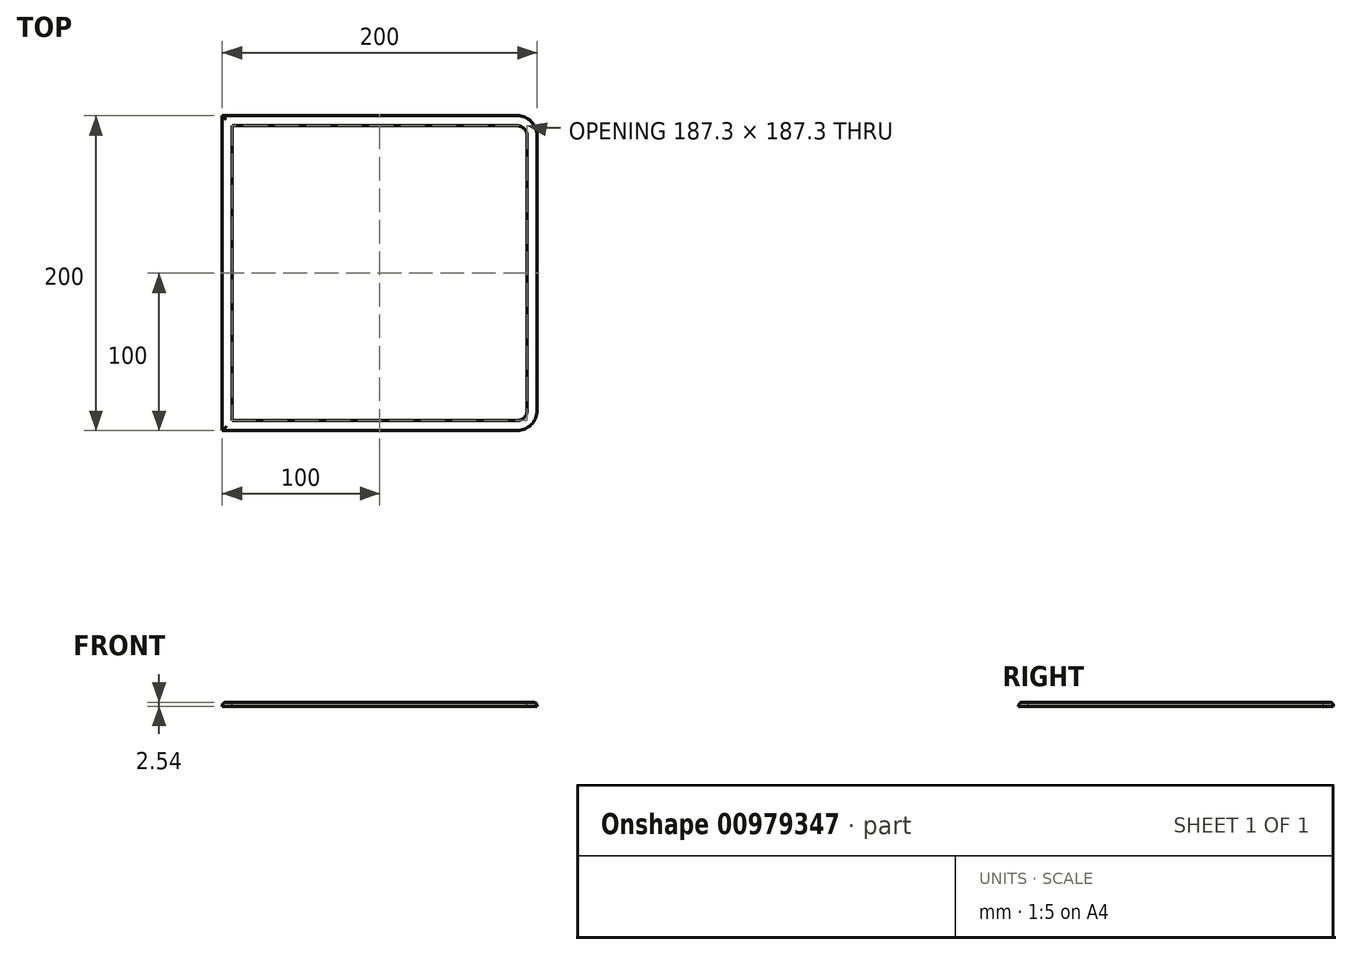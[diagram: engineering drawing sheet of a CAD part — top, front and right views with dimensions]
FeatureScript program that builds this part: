
annotation { "Feature Type Name" : "Feature", "Feature Type Description" : "" }
export const myFeature = defineFeature(function(context is Context, id is Id, definition is map)
    precondition{}
    {
        {
            var Q0;
            Q0=qCreatedBy(makeId("Top.planeOp"),FACE);
            var sketch = newSketch(context, id + "F0", { "sketchPlane" : qUnion([Q0])});
            skLineSegment(sketch, "E0.bottom", {"start": v(0, 0) * mm, "end": v(200, 0) * mm});
            skLineSegment(sketch, "E0.top", {"start": v(0, 200) * mm, "end": v(200, 200) * mm});
            skLineSegment(sketch, "E0.left", {"start": v(0, 0) * mm, "end": v(0, 200) * mm});
            skLineSegment(sketch, "E0.right", {"start": v(200, 0) * mm, "end": v(200, 200) * mm});
            skSolve(sketch);
        }
        {
            var Q0;
            Q0=makeQuery(id+"F0.imprint","IMPRINT",FACE,{"disambiguationData":[TD([[makeQuery(id+"F0.imprint","IMPRINT",EDGE,{"derivedFrom":sQuery(id+"F0.wireOp",EDGE,"E0.bottom")}),1.0]])]});
            extrude(context, id + "F1", {"entities" : qUnion([Q0]), "depth" : 2.54 * mm, "offsetDistance" : 25.4 * mm});
        }
        {
            var Q0;
            Q0=makeQuery(id+"F1.opExtrude","SWEPT_EDGE",EDGE,{"disambiguationData":[OSD([sQuery(id+"F0.wireOp",EDGE,"E0.bottom"),sQuery(id+"F0.wireOp",EDGE,"E0.right")])]});
            var Q1;
            Q1=makeQuery(id+"F1.opExtrude","SWEPT_EDGE",EDGE,{"disambiguationData":[OSD([sQuery(id+"F0.wireOp",EDGE,"E0.top"),sQuery(id+"F0.wireOp",EDGE,"E0.right")])]});
            fillet(context, id + "F2", {"entities" : qUnion([Q0, Q1]), "radius" : 12.7 * mm, "tangentPropagation" : true, "allowEdgeOverflow" : false});
        }
        {
            var Q0;
            Q0=makeQuery(id+"F1.opExtrude","CAP_FACE",FACE,{"disambiguationData":[OSD([sQuery(id+"F0.wireOp",EDGE,"E0.bottom"),sQuery(id+"F0.wireOp",EDGE,"E0.top"),sQuery(id+"F0.wireOp",EDGE,"E0.left"),sQuery(id+"F0.wireOp",EDGE,"E0.right")])],"isStart":false});
            var sketch = newSketch(context, id + "F3", { "sketchPlane" : qUnion([Q0])});
            skLineSegment(sketch, "E1.0", {"start": v(6.35, 6.35) * mm, "end": v(6.35, 193.65) * mm});
            skArc(sketch, "E1.1", {"start": v(193.65, 187.3) * mm, "mid": v(191.8, 191.8) * mm, "end": v(187.3, 193.65) * mm});
            skLineSegment(sketch, "E1.2", {"start": v(193.65, 12.7) * mm, "end": v(193.65, 187.3) * mm});
            skLineSegment(sketch, "E1.3", {"start": v(6.35, 193.65) * mm, "end": v(187.3, 193.65) * mm});
            skArc(sketch, "E1.4", {"start": v(187.3, 6.35) * mm, "mid": v(191.8, 8.2) * mm, "end": v(193.65, 12.7) * mm});
            skLineSegment(sketch, "E1.5", {"start": v(6.35, 6.35) * mm, "end": v(187.3, 6.35) * mm});
            skSolve(sketch);
        }
        {
            var Q0;
            Q0=makeQuery(id+"F3.imprint","IMPRINT",FACE,{"disambiguationData":[TD([[makeQuery(id+"F3.imprint","IMPRINT",EDGE,{"derivedFrom":sQuery(id+"F3.wireOp",EDGE,"E1.0")}),-1.0]])]});
            extrude(context, id + "F4", {"entities" : qUnion([Q0]), "operationType" : NewBodyOperationType.REMOVE, "endBound" : BoundingType.THROUGH_ALL, "oppositeDirection" : true, "depth" : 25.4 * mm, "offsetDistance" : 25.4 * mm});
        }
        {
            var Q0;
            Q0=makeQuery(id+"F4.boolean.opBoolean","COPY",EDGE,{"derivedFrom":makeQuery(id+"F4.opExtrude","CAP_EDGE",EDGE,{"disambiguationData":[OSD([sQuery(id+"F3.wireOp",EDGE,"E1.3")])],"isStart":true})});
            var Q1;
            Q1=makeQuery(id+"F4.boolean.opBoolean","COPY",EDGE,{"derivedFrom":makeQuery(id+"F4.opExtrude","CAP_EDGE",EDGE,{"disambiguationData":[OSD([sQuery(id+"F3.wireOp",EDGE,"E1.0")])],"isStart":true})});
            var Q2;
            {var subQ0=sQuery(id+"F0.wireOp",EDGE,"E0.right");var subQ1=sQuery(id+"F0.wireOp",EDGE,"E0.top");Q2=makeQuery(id+"F2.opFillet","BLEND_EDGE",EDGE,{"blendedFrom":[makeQuery(id+"F1.opExtrude","SWEPT_EDGE",EDGE,{"disambiguationData":[OSD([subQ1,subQ0])]}),makeQuery(id+"F1.opExtrude","CAP_FACE",FACE,{"disambiguationData":[OSD([sQuery(id+"F0.wireOp",EDGE,"E0.bottom"),subQ1,sQuery(id+"F0.wireOp",EDGE,"E0.left"),subQ0])],"isStart":false})],"blendedInto":[makeQuery(id+"F1.opExtrude","CAP_FACE",FACE,{"disambiguationData":[OSD([sQuery(id+"F0.wireOp",EDGE,"E0.bottom"),subQ1,sQuery(id+"F0.wireOp",EDGE,"E0.left"),subQ0])],"isStart":false})]});}
            var Q3;
            Q3=makeQuery(id+"F1.opExtrude","CAP_EDGE",EDGE,{"disambiguationData":[OSD([sQuery(id+"F0.wireOp",EDGE,"E0.left")])],"isStart":false});
            fillet(context, id + "F5", {"entities" : qUnion([Q0, Q1, Q2, Q3]), "radius" : 2.54 * mm, "tangentPropagation" : true, "allowEdgeOverflow" : false});
        }
    });
